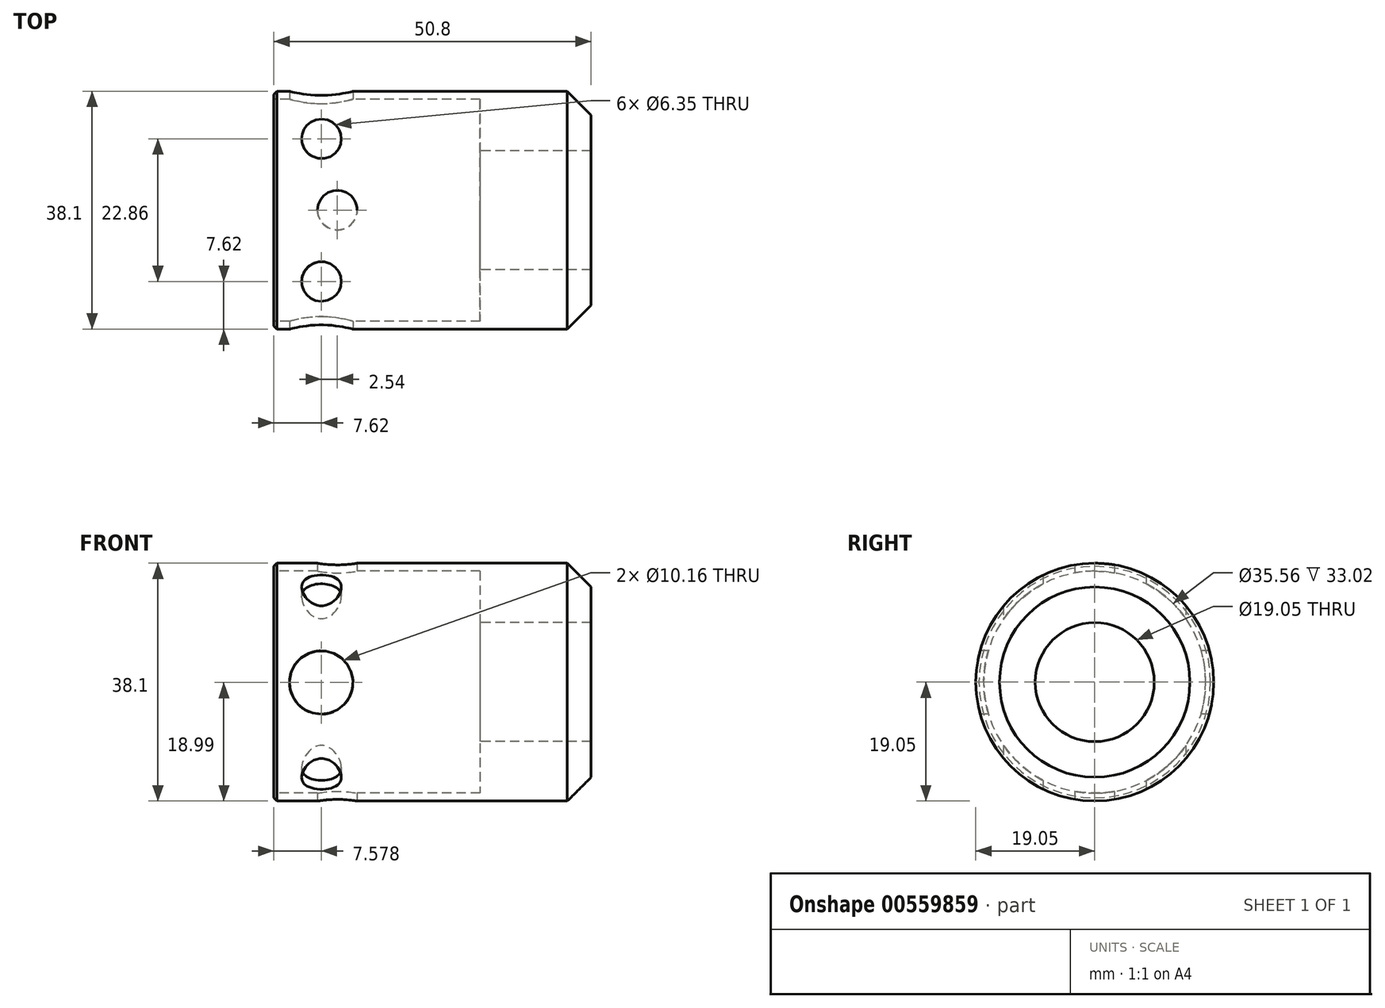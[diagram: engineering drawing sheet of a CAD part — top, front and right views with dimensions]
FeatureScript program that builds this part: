
annotation { "Feature Type Name" : "Feature", "Feature Type Description" : "" }
export const myFeature = defineFeature(function(context is Context, id is Id, definition is map)
    precondition{}
    {
        {
            var Q0;
            Q0=qCreatedBy(makeId("Right.planeOp"),FACE);
            var sketch = newSketch(context, id + "F0", { "sketchPlane" : qUnion([Q0])});
            skCircle(sketch, "E0", {"center": v(19.05, 19.05) * mm, "radius": 19.05 * mm});
            skSolve(sketch);
        }
        {
            var Q0;
            Q0 = qSketchRegion(id + "F0", true);
            extrude(context, id + "F1", {"entities" : qUnion([Q0]), "depth" : 50.8 * mm, "offsetDistance" : 25.4 * mm});
        }
        {
            var Q0;
            Q0=qCreatedBy(makeId("Top.planeOp"),FACE);
            var sketch = newSketch(context, id + "F2", { "sketchPlane" : qUnion([Q0])});
            skPoint(sketch, "E1", {"position": v(7.62, 30.48) * mm});
            skPoint(sketch, "E2", {"position": v(7.62, 7.62) * mm});
            skPoint(sketch, "E3", {"position": v(10.16, 19.05) * mm});
            skSolve(sketch);
        }
        {
            var Q0;
            Q0=sQuery(id+"F2.wireOp",VERTEX,"E3");
            var Q1;
            Q1=sQuery(id+"F2.wireOp",VERTEX,"E2");
            var Q2;
            Q2=sQuery(id+"F2.wireOp",VERTEX,"E1");
            var Q3;
            Q3=makeQuery(id+"F1.opExtrude","SWEPT_BODY",BODY,{"disambiguationData":[OSD([sQuery(id+"F0.wireOp",EDGE,"E0")])]});
            hole(context, id + "F3", {"style" : HoleStyle.SIMPLE, "endStyle" : HoleEndStyle.THROUGH, "oppositeDirection" : true, "holeDiameter" : 6.35 * mm, "isTappedThrough" : true, "tappedDepth" : 12.7 * mm, "tapClearance" : 3, "locations" : qUnion([Q0, Q1, Q2]), "scope" : qUnion([Q3])});
        }
        {
            var Q0;
            Q0=qCreatedBy(makeId("Top.planeOp"),FACE);
            var sketch = newSketch(context, id + "F4", { "sketchPlane" : qUnion([Q0])});
            skLineSegment(sketch, "E4", {"start": v(0, 0) * mm, "end": v(28.27, 0) * mm});
            skLineSegment(sketch, "E5", {"start": v(28.27, 0) * mm, "end": v(24.2, 0) * mm});
            skSolve(sketch);
        }
        {
            var Q0;
            Q0=qCreatedBy(makeId("Front.planeOp"),FACE);
            var sketch = newSketch(context, id + "F5", { "sketchPlane" : qUnion([Q0])});
            skPoint(sketch, "E6", {"position": v(7.58, 19) * mm});
            skSolve(sketch);
        }
        {
            var Q0;
            Q0=sQuery(id+"F5.wireOp",VERTEX,"E6");
            var Q1;
            Q1=makeQuery(id+"F1.opExtrude","SWEPT_BODY",BODY,{"disambiguationData":[OSD([sQuery(id+"F0.wireOp",EDGE,"E0")])]});
            hole(context, id + "F6", {"style" : HoleStyle.SIMPLE, "endStyle" : HoleEndStyle.THROUGH, "holeDiameter" : 10.16 * mm, "isTappedThrough" : true, "tappedDepth" : 12.7 * mm, "tapClearance" : 3, "locations" : qUnion([Q0]), "scope" : qUnion([Q1])});
        }
        {
            var Q0;
            Q0=makeQuery(id+"F1.opExtrude","CAP_FACE",FACE,{"disambiguationData":[OSD([sQuery(id+"F0.wireOp",EDGE,"E0")])],"isStart":true});
            var sketch = newSketch(context, id + "F7", { "sketchPlane" : qUnion([Q0])});
            skCircle(sketch, "E7", {"center": v(-19.05, 19.05) * mm, "radius": 17.78 * mm});
            skSolve(sketch);
        }
        {
            var Q0;
            Q0 = qSketchRegion(id + "F7", true);
            extrude(context, id + "F8", {"entities" : qUnion([Q0]), "operationType" : NewBodyOperationType.REMOVE, "oppositeDirection" : true, "depth" : 33.02 * mm, "offsetDistance" : 25.4 * mm});
        }
        {
            var Q0;
            Q0=qCreatedBy(makeId("Right.planeOp"),FACE);
            var sketch = newSketch(context, id + "F9", { "sketchPlane" : qUnion([Q0])});
            skCircle(sketch, "E8", {"center": v(19.05, 19.05) * mm, "radius": 6.35 * mm});
            skSolve(sketch);
        }
        {
            var Q0;
            Q0=sQuery(id+"F9.wireOp",VERTEX,"E8.center");
            var Q1;
            Q1=makeQuery(id+"F1.opExtrude","SWEPT_BODY",BODY,{"disambiguationData":[OSD([sQuery(id+"F0.wireOp",EDGE,"E0")])]});
            hole(context, id + "F10", {"style" : HoleStyle.SIMPLE, "endStyle" : HoleEndStyle.THROUGH, "oppositeDirection" : true, "holeDiameter" : 19.05 * mm, "isTappedThrough" : true, "tappedDepth" : 12.7 * mm, "tapClearance" : 3, "locations" : qUnion([Q0]), "scope" : qUnion([Q1])});
        }
        {
            var Q0;
            Q0=makeQuery(id+"F1.opExtrude","CAP_EDGE",EDGE,{"disambiguationData":[OSD([sQuery(id+"F0.wireOp",EDGE,"E0")])],"isStart":false});
            chamfer(context, id + "F11", {"entities" : qUnion([Q0]), "width" : 3.8 * mm, "tangentPropagation" : true});
        }
        {
            var Q0;
            Q0=qCreatedBy(makeId("Top.planeOp"),FACE);
            var sketch = newSketch(context, id + "F12", { "sketchPlane" : qUnion([Q0])});
            skLineSegment(sketch, "E9.bottom", {"start": v(19.97, 11.51) * mm, "end": v(40.61, 11.51) * mm});
            skLineSegment(sketch, "E9.top", {"start": v(19.97, 21.95) * mm, "end": v(40.61, 21.95) * mm});
            skLineSegment(sketch, "E9.left", {"start": v(19.97, 11.51) * mm, "end": v(19.97, 21.95) * mm});
            skLineSegment(sketch, "E9.right", {"start": v(40.61, 11.51) * mm, "end": v(40.61, 21.95) * mm});
            skSolve(sketch);
        }
        {
            var Q0;
            Q0 = qSketchRegion(id + "F12", true);
            extrude(context, id + "F13", {"entities" : qUnion([Q0]), "operationType" : NewBodyOperationType.REMOVE, "oppositeDirection" : true, "depth" : 5.08 * mm, "offsetDistance" : 25.4 * mm});
        }
        {
            var Q0;
            Q0=makeQuery(id+"F1.opExtrude","CAP_EDGE",EDGE,{"disambiguationData":[OSD([sQuery(id+"F0.wireOp",EDGE,"E0")])],"isStart":true});
            chamfer(context, id + "F14", {"entities" : qUnion([Q0]), "width" : 0.5 * mm, "tangentPropagation" : true});
        }
    });
